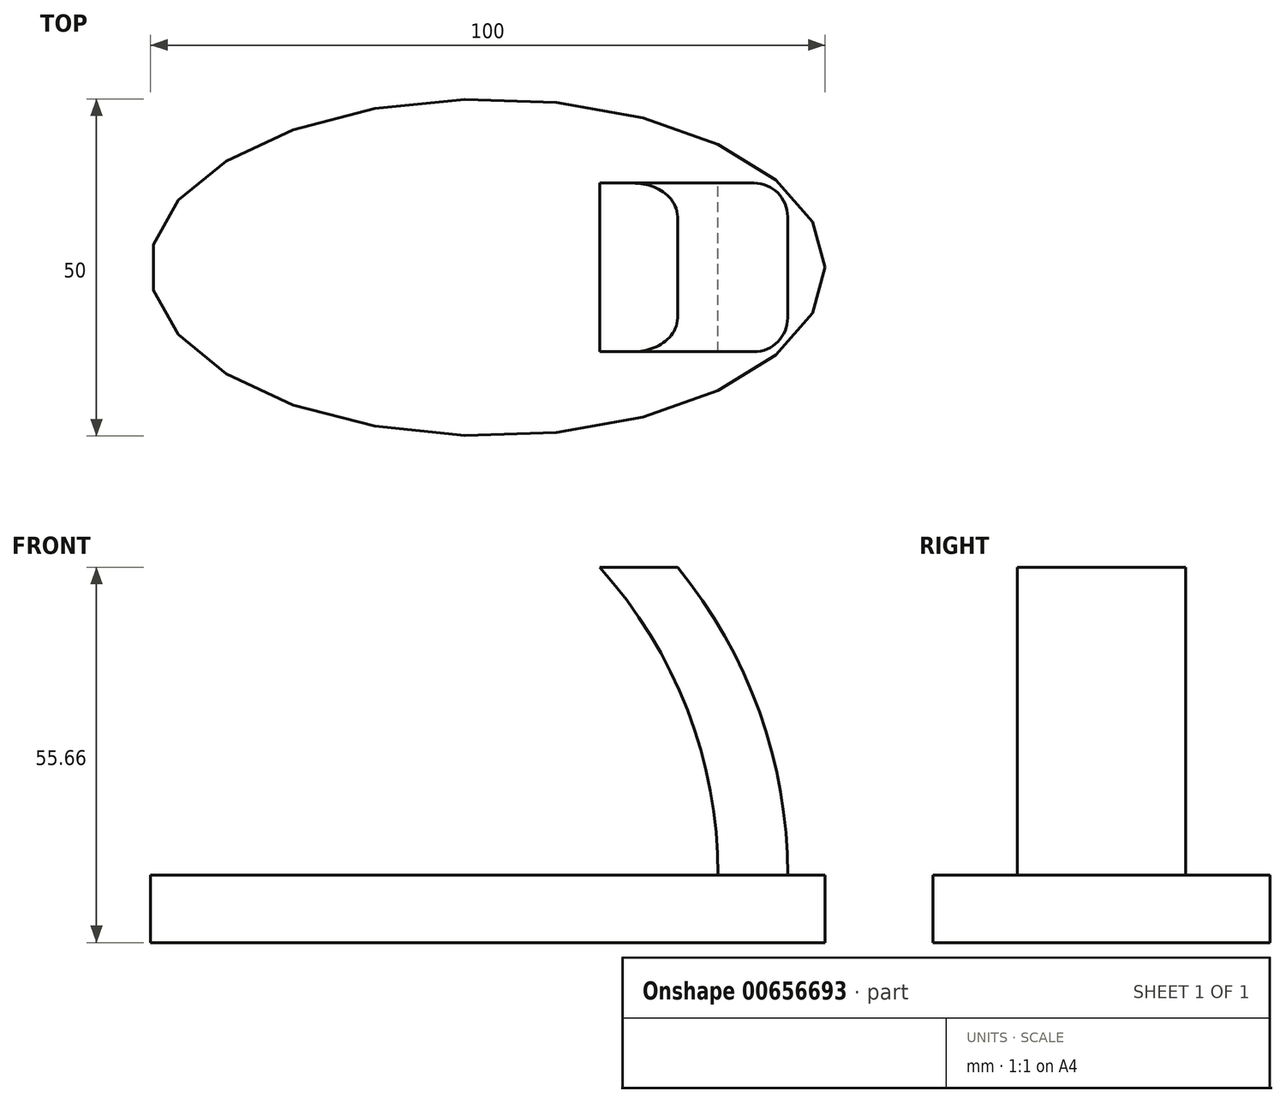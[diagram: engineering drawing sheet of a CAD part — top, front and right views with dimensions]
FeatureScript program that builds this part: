
annotation { "Feature Type Name" : "Feature", "Feature Type Description" : "" }
export const myFeature = defineFeature(function(context is Context, id is Id, definition is map)
    precondition{}
    {
        {
            var Q0;
            Q0=qCreatedBy(makeId("Top.planeOp"),FACE);
            var sketch = newSketch(context, id + "F0", { "sketchPlane" : qUnion([Q0])});
            skEllipse(sketch, "E0", {"center": v(0, 0) * mm, "majorRadius": 50 * mm, "minorRadius": 25 * mm, "majorAxis": v(1, 0)});
            skSolve(sketch);
        }
        {
            var Q0;
            Q0 = qSketchRegion(id + "F0", true);
            extrude(context, id + "F1", {"entities" : qUnion([Q0]), "depth" : 10 * mm, "offsetDistance" : 25 * mm});
        }
        {
            var Q0;
            Q0=qCreatedBy(makeId("Front.planeOp"),FACE);
            var sketch = newSketch(context, id + "F2", { "sketchPlane" : qUnion([Q0])});
            skArc(sketch, "E1", {"start": v(44.47, 10.06) * mm, "mid": v(40.26, 34.28) * mm, "end": v(28.13, 55.66) * mm});
            skArc(sketch, "E2", {"start": v(34.14, 10.06) * mm, "mid": v(29.6, 34.5) * mm, "end": v(16.58, 55.66) * mm});
            skLineSegment(sketch, "E3", {"start": v(16.58, 55.66) * mm, "end": v(28.13, 55.66) * mm});
            skPoint(sketch, "E4.orphan", {"position": v(0, 55.66) * mm});
            skLineSegment(sketch, "E5", {"start": v(34.14, 10.06) * mm, "end": v(44.47, 10.06) * mm});
            skSolve(sketch);
        }
        {
            var Q0;
            Q0 = qSketchRegion(id + "F2", true);
            extrude(context, id + "F3", {"entities" : qUnion([Q0]), "endBound" : BoundingType.SYMMETRIC, "depth" : 25 * mm, "offsetDistance" : 25 * mm});
        }
        {
            var Q0;
            Q0=makeQuery(id+"F3.opExtrude","CAP_EDGE",EDGE,{"disambiguationData":[OSD([sQuery(id+"F2.wireOp",EDGE,"E1")])],"isStart":false});
            var Q1;
            Q1=makeQuery(id+"F3.opExtrude","CAP_EDGE",EDGE,{"disambiguationData":[OSD([sQuery(id+"F2.wireOp",EDGE,"E1")])],"isStart":true});
            fillet(context, id + "F4", {"entities" : qUnion([Q0, Q1]), "radius" : 5 * mm, "tangentPropagation" : true, "allowEdgeOverflow" : false});
        }
        {
            var Q0;
            Q0=makeQuery(id+"F3.opExtrude","SWEPT_FACE",FACE,{"disambiguationData":[OSD([sQuery(id+"F2.wireOp",EDGE,"E5")])]});
            extrude(context, id + "F5", {"entities" : qUnion([Q0]), "operationType" : NewBodyOperationType.ADD, "depth" : 2 * mm, "offsetDistance" : 25 * mm});
        }
    });
